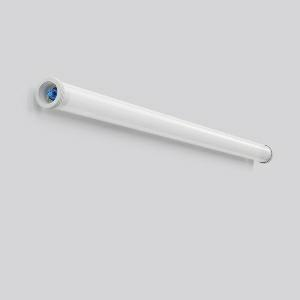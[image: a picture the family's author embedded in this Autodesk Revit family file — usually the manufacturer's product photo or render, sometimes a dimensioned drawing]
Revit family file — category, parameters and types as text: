
# Revit family: planox_tube_601072_002_1_4d05
name_source: partatom
category: Lighting Fixtures
units: mm (PartAtom-declared; Revit-internal decimal feet)

## family parameters
Cut with Voids When Loaded = No
Host = Face
Light Source = No
Part Type = Normal
Room Calculation Point = No
Round Connector Dimension = Use Diameter
Shared = No

## types (1)
- PLANOX TUBE (1 x LED Modul 840, 8650 lm, 4000)
    Apparent Load = 62 VA
    CIE Flux Codes = 42 71 90 91 100
    Color Rendering = 80
    Color Temperature = 4000
    Default Elevation = 1800 mm
    Description = Series: PLANOX TUBE
Robust protective tube luminaire for tough requirements. Rack made of sheet steel, white powder coated. End caps made of plastic (polyamide) grey. Diffuser made of plastic (polycarbonate), opal, shockproof. Symmetrical light distribution. Homogeneous light distribution. With accessories for wall, ceiling or pendant mounting. Driver integrated. Easy installation with the Plug+Play Wieland RST CLASSIC plug-in system. Luminaire with integrated through-wiring for series connection of further luminaires by two Wieland RST Classic plug connectors (plug and socket). Accessories for electrical connection must be ordered separately. Mounting set must be ordered separately. Luminaire with limited surface temperature in accordance with EN 60598-2-24 for use in environments in which a deposit of conductive dust on the luminaire can be expected. Qualified for use in the food and drink industry. Suitable for lighting in public car parks and public off-street parking spaces according to DIN 67528. Environmentally friendly and resource-saving due to replaceable components. 
Colour: white
Diameter: 78 mm
Length: 1564 mm
Lamp: LED
Socket: without socket
Colour temperature: 4000K
Colour rendering index (CRI): 83
System power: 62 W
Rated luminous flux: 8650 lm
Luminous efficiency: 140 lm/W
Control gear: Regulated power supply
Protection class: I
Type of protection: IP 67
    Height = 0 mm  [stored 0 ft]
    Lamp = 1 x LED Modul 840
    Lamp Light Flux = 8650 lm
    Lamp count = 1
    Length = 1564 mm
    Lifetime = 50000 h
    Luminous efficacy = 140 lm/W
    Manufacturer = RZB
    ModVariant = No
    Model = 601072.002.1
    Mounting Place = Ceiling
    Mounting Type = Surface mounted
    Number of Poles = 1
    OnlyDefault = Yes
    Power Factor = 1
    Product Name = PLANOX TUBE
    Product group = Surface mounted luminaires for moist/humid enviroments
    ProductGroupID = 308
    Protection Class = Protection class I
    Protection Degree = Degree of protection
    RLX_Detail_Level = 1
    RLX_Emergency_Light_Flux = 0 lm
    RLX_Emergency_Type = 0
    RLX_Emergency_Type_DB = No
    RlxData = <blob elided: 35197 chars, md5=4b4bf992>
    Socket = socket
    Standby Power = 0 W
    System Light Flux = 8650 lm
    System Power = 62 W
    Type Comments = Product without accessories
    Type Image = 601072.002.jpg
    URL = http://relux.com
    VarID = ---
    Voltage = 0 V
    Weight = 0.00 kg
    Width = 0 mm  [stored 0 ft]

note: [stored X ft] marks values corroborated as IEEE doubles in the binary element streams (Revit-internal decimal feet)

## geometry (parser evidence)
native form markers: Blend x4, Sweep x14
no freeform markers — native parametric forms only
